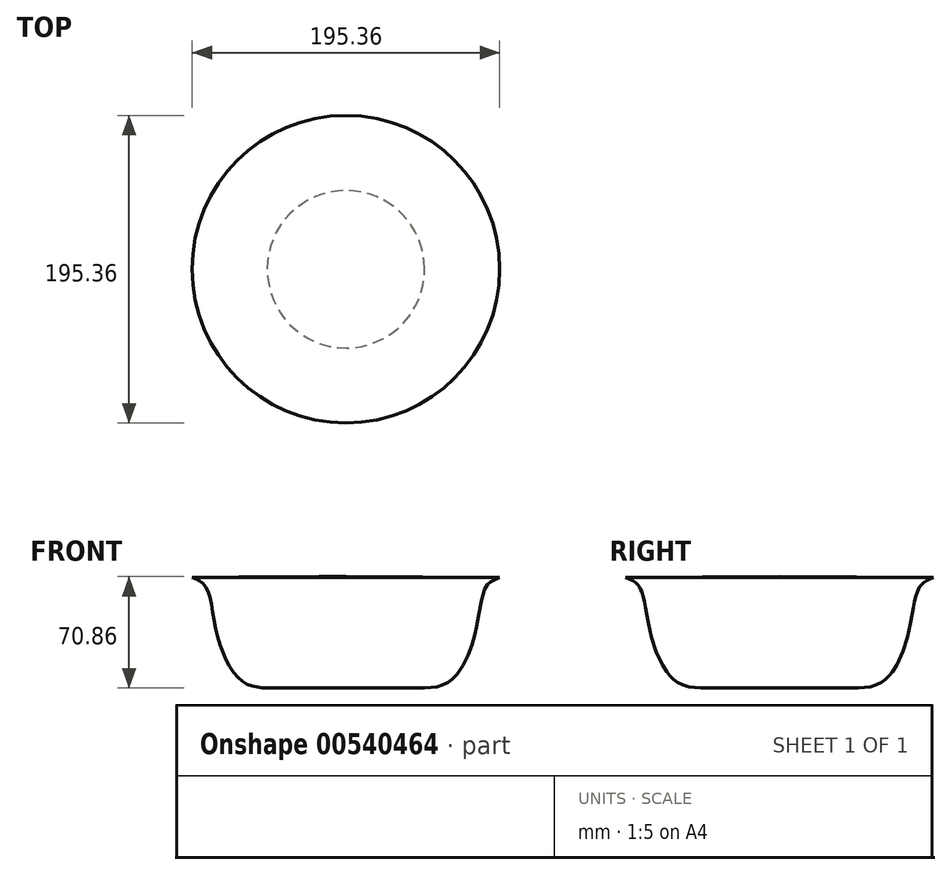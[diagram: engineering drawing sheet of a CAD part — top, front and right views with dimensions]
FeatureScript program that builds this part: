
annotation { "Feature Type Name" : "Feature", "Feature Type Description" : "" }
export const myFeature = defineFeature(function(context is Context, id is Id, definition is map)
    precondition{}
    {
        {
            var Q0;
            Q0=qCreatedBy(makeId("Front.planeOp"),FACE);
            var sketch = newSketch(context, id + "F0", { "sketchPlane" : qUnion([Q0])});
            skLineSegment(sketch, "E0", {"start": v(0, 0) * mm, "end": v(-50, 0) * mm});
            skLineSegment(sketch, "E1", {"start": v(0, 0) * mm, "end": v(0, 70.86) * mm});
            skLineSegment(sketch, "E2", {"start": v(0, 70.86) * mm, "end": v(-97.68, 70.27) * mm});
            skFitSpline(sketch, "E3", {"points": [v(-50, 0) * mm, v(-65.66, 4.15) * mm, v(-81.46, 32.58) * mm, v(-89.08, 64.36) * mm, v(-97.68, 70.27) * mm], "startDerivative": vector(-75.26, 4.67) * mm, "endDerivative": vector(-55.72, 21.02) * mm});
            skSolve(sketch);
        }
        {
            var Q0;
            Q0=makeQuery(id+"F0.imprint","IMPRINT",FACE,{"disambiguationData":[TD([[makeQuery(id+"F0.imprint","IMPRINT",EDGE,{"derivedFrom":sQuery(id+"F0.wireOp",EDGE,"E0")}),-1.0]])]});
            var Q1;
            Q1=sQuery(id+"F0.wireOp",EDGE,"E1");
            revolve(context, id + "F1", {"entities" : qUnion([Q0]), "axis" : qUnion([Q1]), "revolveType" : RevolveType.FULL});
        }
    });
